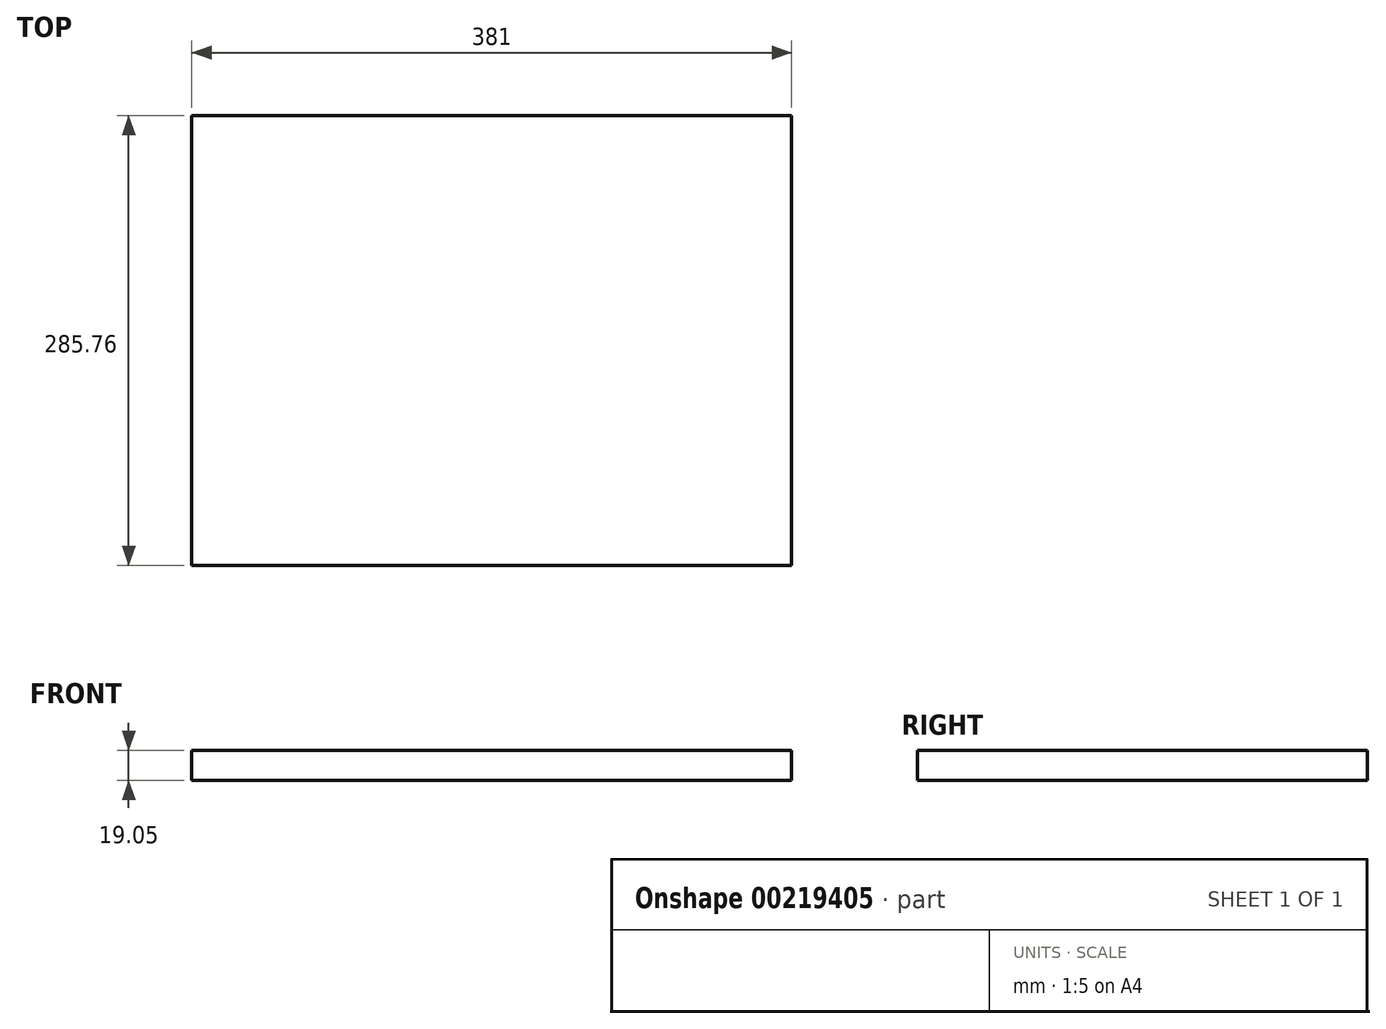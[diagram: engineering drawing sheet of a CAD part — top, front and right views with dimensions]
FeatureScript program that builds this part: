
annotation { "Feature Type Name" : "Feature", "Feature Type Description" : "" }
export const myFeature = defineFeature(function(context is Context, id is Id, definition is map)
    precondition{}
    {
        {
            var Q0;
            Q0=qCreatedBy(makeId("Top.planeOp"),FACE);
            var sketch = newSketch(context, id + "F0", { "sketchPlane" : qUnion([Q0])});
            skLineSegment(sketch, "E0.bottom", {"start": v(190.5, -142.88) * mm, "end": v(-190.5, -142.88) * mm});
            skLineSegment(sketch, "E0.top", {"start": v(190.5, 142.88) * mm, "end": v(-190.5, 142.88) * mm});
            skLineSegment(sketch, "E0.left", {"start": v(190.5, -142.88) * mm, "end": v(190.5, 142.88) * mm});
            skLineSegment(sketch, "E0.right", {"start": v(-190.5, -142.88) * mm, "end": v(-190.5, 142.88) * mm});
            skPoint(sketch, "E0.middle", {"position": v(0, 0) * mm});
            skSolve(sketch);
        }
        {
            var Q0;
            Q0=makeQuery(id+"F0.imprint","IMPRINT",FACE,{"disambiguationData":[TD([[makeQuery(id+"F0.imprint","IMPRINT",EDGE,{"derivedFrom":sQuery(id+"F0.wireOp",EDGE,"E0.bottom")}),-1.0]])]});
            extrude(context, id + "F1", {"entities" : qUnion([Q0]), "depth" : 19.05 * mm, "offsetDistance" : 25.4 * mm});
        }
    });
